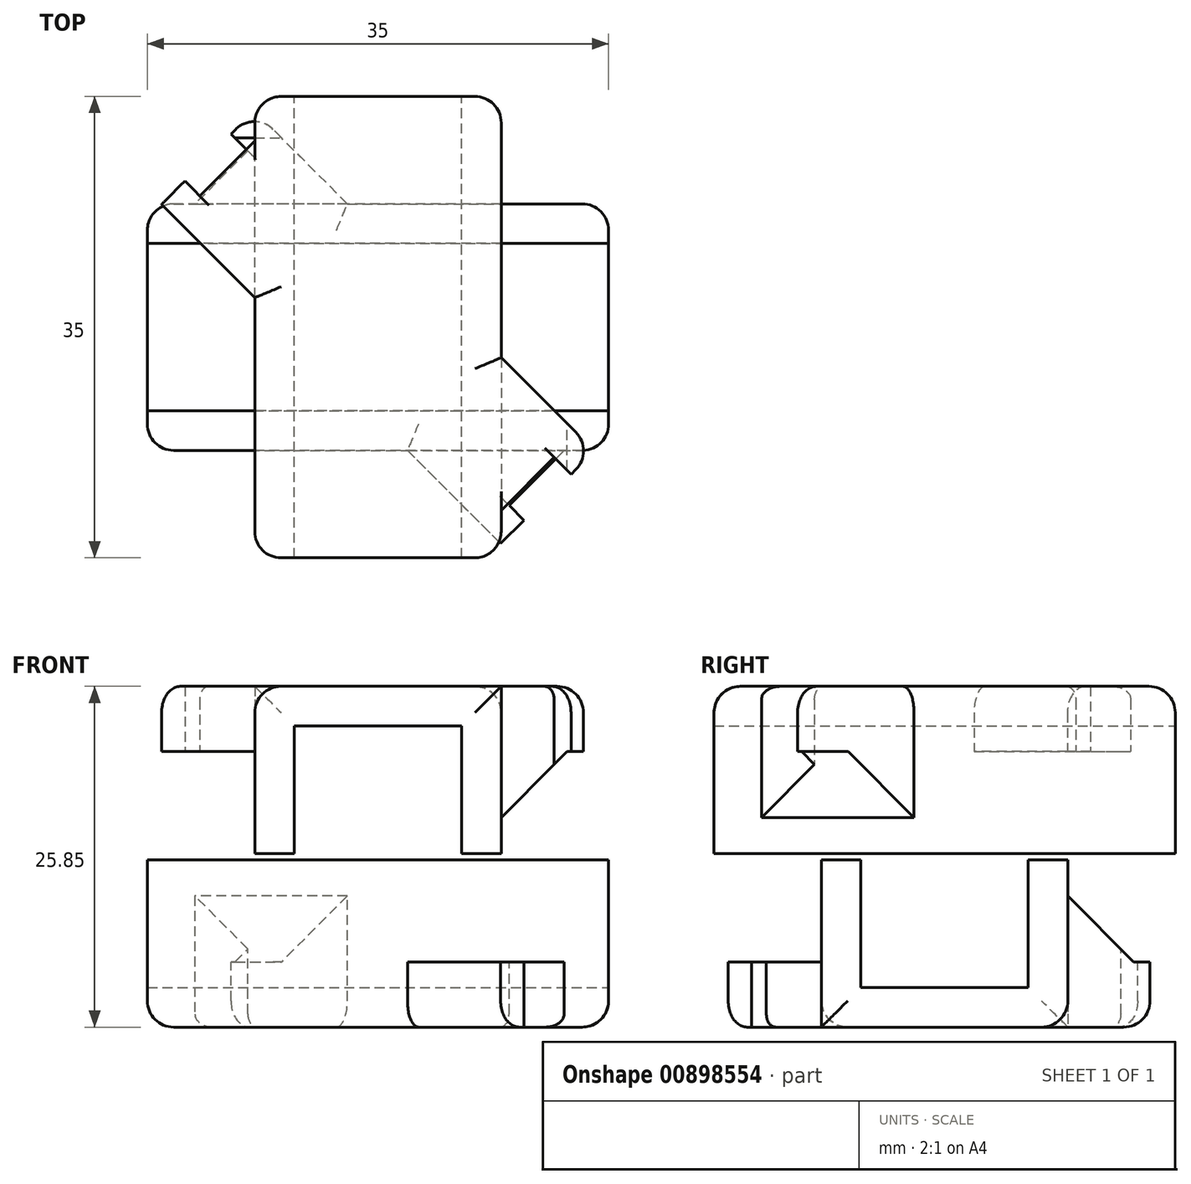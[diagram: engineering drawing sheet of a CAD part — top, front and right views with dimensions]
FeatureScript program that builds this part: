
annotation { "Feature Type Name" : "Feature", "Feature Type Description" : "" }
export const myFeature = defineFeature(function(context is Context, id is Id, definition is map)
    precondition{}
    {
        {
            var Q0;
            Q0=qCreatedBy(makeId("Front.planeOp"),FACE);
            var sketch = newSketch(context, id + "F0", { "sketchPlane" : qUnion([Q0])});
            skLineSegment(sketch, "E0.bottom", {"start": v(6.35, -6.35) * mm, "end": v(-6.35, -6.35) * mm});
            skLineSegment(sketch, "E0.top", {"start": v(6.35, 6.35) * mm, "end": v(-6.35, 6.35) * mm});
            skLineSegment(sketch, "E0.left", {"start": v(6.35, -6.35) * mm, "end": v(6.35, 6.35) * mm});
            skLineSegment(sketch, "E0.right", {"start": v(-6.35, -6.35) * mm, "end": v(-6.35, 6.35) * mm});
            skPoint(sketch, "E0.middle", {"position": v(0, 0) * mm});
            skLineSegment(sketch, "E1.0", {"start": v(9.35, -9.35) * mm, "end": v(-9.35, -9.35) * mm});
            skLineSegment(sketch, "E1.1", {"start": v(9.35, -9.35) * mm, "end": v(9.35, 9.35) * mm});
            skLineSegment(sketch, "E1.2", {"start": v(9.35, 9.35) * mm, "end": v(-9.35, 9.35) * mm});
            skLineSegment(sketch, "E1.3", {"start": v(-9.35, -9.35) * mm, "end": v(-9.35, 9.35) * mm});
            skLineSegment(sketch, "E2", {"start": v(0, 0) * mm, "end": v(0, 32.23) * mm, "construction": true});
            skSolve(sketch);
        }
        {
            var Q0;
            Q0 = qSketchRegion(id + "F0", true);
            extrude(context, id + "F1", {"entities" : qUnion([Q0]), "depth" : 35 * mm, "offsetDistance" : 25 * mm, "symmetric" : true});
        }
        {
            var Q0;
            Q0=qCreatedBy(makeId("Front.planeOp"),FACE);
            var sketch = newSketch(context, id + "F2", { "sketchPlane" : qUnion([Q0])});
            skLineSegment(sketch, "E3.bottom", {"start": v(6.35, -6.35) * mm, "end": v(-6.35, -6.35) * mm, "construction": true});
            skLineSegment(sketch, "E3.top", {"start": v(6.35, 6.35) * mm, "end": v(-6.35, 6.35) * mm, "construction": true});
            skLineSegment(sketch, "E3.left", {"start": v(6.35, -6.35) * mm, "end": v(6.35, 6.35) * mm, "construction": true});
            skLineSegment(sketch, "E3.right", {"start": v(-6.35, -6.35) * mm, "end": v(-6.35, 6.35) * mm, "construction": true});
            skPoint(sketch, "E3.middle", {"position": v(0, 0) * mm});
            skLineSegment(sketch, "E4.bottom", {"start": v(20.53, -3.33) * mm, "end": v(-20.53, -3.33) * mm});
            skLineSegment(sketch, "E4.top", {"start": v(20.53, -26.42) * mm, "end": v(-20.53, -26.42) * mm});
            skLineSegment(sketch, "E4.left", {"start": v(20.53, -3.33) * mm, "end": v(20.53, -26.42) * mm});
            skLineSegment(sketch, "E4.right", {"start": v(-20.53, -3.33) * mm, "end": v(-20.53, -26.42) * mm});
            skPoint(sketch, "E4.middle", {"position": v(0, -14.87) * mm});
            skSolve(sketch);
        }
        {
            var Q0;
            Q0 = qSketchRegion(id + "F2", true);
            extrude(context, id + "F3", {"entities" : qUnion([Q0]), "operationType" : NewBodyOperationType.REMOVE, "depth" : 39.8 * mm, "offsetDistance" : 25 * mm, "symmetric" : true});
        }
        {
            var Q0;
            Q0=qCreatedBy(makeId("Top.planeOp"),FACE);
            var sketch = newSketch(context, id + "F4", { "sketchPlane" : qUnion([Q0])});
            skLineSegment(sketch, "E5.bottom", {"start": v(-9.35, 16.38) * mm, "end": v(-16.42, 9.3) * mm});
            skLineSegment(sketch, "E5.top", {"start": v(16.42, -9.39) * mm, "end": v(9.35, -16.46) * mm});
            skLineSegment(sketch, "E5.left", {"start": v(-9.35, 16.38) * mm, "end": v(16.42, -9.39) * mm});
            skLineSegment(sketch, "E5.right", {"start": v(-16.42, 9.3) * mm, "end": v(9.35, -16.46) * mm});
            skPoint(sketch, "E5.middle", {"position": v(0, -0.04) * mm});
            skLineSegment(sketch, "E6.bottom", {"start": v(-10, 13.49) * mm, "end": v(-13.53, 9.95) * mm});
            skLineSegment(sketch, "E6.right", {"start": v(-13.53, 9.95) * mm, "end": v(-15.78, 12.2) * mm});
            skPoint(sketch, "E6.middle", {"position": v(-12.89, 12.85) * mm});
            skLineSegment(sketch, "E7.top", {"start": v(13.37, -9.87) * mm, "end": v(9.83, -13.4) * mm});
            skLineSegment(sketch, "E7.left", {"start": v(15.93, -12.44) * mm, "end": v(13.37, -9.87) * mm});
            skPoint(sketch, "E7.middle", {"position": v(12.88, -12.92) * mm});
            skLineSegment(sketch, "E8", {"start": v(-10, 13.49) * mm, "end": v(-5.5, 17.98) * mm});
            skLineSegment(sketch, "E9", {"start": v(9.83, -13.4) * mm, "end": v(5.07, -18.17) * mm});
            skLineSegment(sketch, "E10", {"start": v(0, 0) * mm, "end": v(0, 33.96) * mm, "construction": true});
            skSolve(sketch);
        }
        {
            var Q0;
            {var subQ15=sQuery(id+"F4.wireOp",EDGE,"E6.bottom");Q0=makeQuery(id+"F4.imprint","IMPRINT",FACE,{"disambiguationData":[TD([[makeQuery(id+"F4.imprint","IMPRINT",EDGE,{"derivedFrom":subQ15}),1.0]])]});}
            extrude(context, id + "F5", {"entities" : qUnion([Q0]), "operationType" : NewBodyOperationType.ADD, "depth" : ((12.7 / 2) + 3) * mm, "offsetDistance" : 25 * mm, "hasSecondDirection" : true, "secondDirectionOppositeDirection" : false, "secondDirectionDepth" : 4.4 * mm});
        }
        {
            var Q0;
            Q0=makeQuery(id+"F5.opExtrude","CAP_EDGE",EDGE,{"disambiguationData":[OSD([sQuery(id+"F4.wireOp",EDGE,"E7.top"),sQuery(id+"F4.wireOp",EDGE,"E9")])],"isStart":false});
            var Q1;
            Q1=makeQuery(id+"F5.opExtrude","CAP_EDGE",EDGE,{"disambiguationData":[OSD([sQuery(id+"F4.wireOp",EDGE,"E6.bottom"),sQuery(id+"F4.wireOp",EDGE,"E8")])],"isStart":false});
            fillet(context, id + "F6", {"entities" : qUnion([Q0, Q1]), "radius" : 1 * mm, "tangentPropagation" : true, "allowEdgeOverflow" : false});
        }
        {
            var Q0;
            Q0=makeQuery(id+"F0.imprint","IMPRINT",FACE,{"disambiguationData":[TD([[makeQuery(id+"F0.imprint","IMPRINT",EDGE,{"derivedFrom":sQuery(id+"F0.wireOp",EDGE,"E0.bottom")}),-1.0]])]});
            var Q1;
            Q1=sQuery(id+"F0.wireOp",EDGE,"E0.bottom");
            var Q2;
            Q2=sQuery(id+"F0.wireOp",EDGE,"E0.top");
            var Q3;
            Q3=sQuery(id+"F0.wireOp",EDGE,"E0.right");
            var Q4;
            Q4=sQuery(id+"F0.wireOp",EDGE,"E0.left");
            extrude(context, id + "F7", {"entities" : qUnion([Q0]), "operationType" : NewBodyOperationType.REMOVE, "surfaceEntities" : qUnion([Q1, Q2, Q3, Q4]), "depth" : 50 * mm, "offsetDistance" : 25 * mm, "symmetric" : true});
        }
        {
            var Q0;
            Q0=makeQuery(id+"F5.boolean.opBoolean","INTERSECT",EDGE,{"derivedFrom":[makeQuery(id+"F1.opExtrude","SWEPT_FACE",FACE,{"disambiguationData":[OSD([sQuery(id+"F0.wireOp",EDGE,"E1.1")])]}),makeQuery(id+"F5.opExtrude","CAP_FACE",FACE,{"disambiguationData":[OSD([sQuery(id+"F4.wireOp",EDGE,"E5.bottom"),sQuery(id+"F4.wireOp",EDGE,"E5.top"),sQuery(id+"F4.wireOp",EDGE,"E5.left"),sQuery(id+"F4.wireOp",EDGE,"E5.right"),sQuery(id+"F4.wireOp",EDGE,"E6.bottom"),sQuery(id+"F4.wireOp",EDGE,"E6.right"),sQuery(id+"F4.wireOp",EDGE,"E7.top"),sQuery(id+"F4.wireOp",EDGE,"E7.left"),sQuery(id+"F4.wireOp",EDGE,"E8"),sQuery(id+"F4.wireOp",EDGE,"E9")])],"isStart":true})]});
            chamfer(context, id + "F8", {"entities" : qUnion([Q0]), "width" : 5 * mm, "tangentPropagation" : true});
        }
        {
            var Q0;
            {var subQ0=sQuery(id+"F4.wireOp",EDGE,"E5.left");var subQ1=sQuery(id+"F0.wireOp",EDGE,"E1.2");var subQ2=sQuery(id+"F0.wireOp",EDGE,"E1.1");Q0=makeQuery(id+"F5.boolean.opBoolean","SPLIT",EDGE,{"disambiguationData":[TD([makeQuery(id+"F5.opExtrude","SWEPT_FACE",FACE,{"disambiguationData":[OSD([subQ0])]})])],"derivedFrom":makeQuery(id+"F1.opExtrude","SWEPT_EDGE",EDGE,{"disambiguationData":[OSD([subQ2,subQ1])]})});}
            var Q1;
            {var subQ0=sQuery(id+"F4.wireOp",EDGE,"E5.right");var subQ1=sQuery(id+"F0.wireOp",EDGE,"E1.2");var subQ2=sQuery(id+"F0.wireOp",EDGE,"E1.3");Q1=makeQuery(id+"F5.boolean.opBoolean","SPLIT",EDGE,{"disambiguationData":[TD([makeQuery(id+"F5.opExtrude","SWEPT_FACE",FACE,{"disambiguationData":[OSD([subQ0])]})])],"derivedFrom":makeQuery(id+"F1.opExtrude","SWEPT_EDGE",EDGE,{"disambiguationData":[OSD([subQ1,subQ2])]})});}
            var Q2;
            Q2=makeQuery(id+"F1.opExtrude","CAP_EDGE",EDGE,{"disambiguationData":[OSD([sQuery(id+"F0.wireOp",EDGE,"E1.2")])],"isStart":false});
            var Q3;
            Q3=makeQuery(id+"F1.opExtrude","CAP_EDGE",EDGE,{"disambiguationData":[OSD([sQuery(id+"F0.wireOp",EDGE,"E1.2")])],"isStart":true});
            var Q4;
            Q4=makeQuery(id+"F5.opExtrude","SWEPT_EDGE",EDGE,{"disambiguationData":[OSD([sQuery(id+"F4.wireOp",EDGE,"E5.top"),sQuery(id+"F4.wireOp",EDGE,"E5.left")])]});
            var Q5;
            Q5=makeQuery(id+"F5.opExtrude","CAP_EDGE",EDGE,{"disambiguationData":[OSD([sQuery(id+"F4.wireOp",EDGE,"E5.left")])],"isStart":false});
            var Q6;
            Q6=makeQuery(id+"F5.opExtrude","CAP_EDGE",EDGE,{"disambiguationData":[OSD([sQuery(id+"F4.wireOp",EDGE,"E5.right")])],"isStart":false});
            var Q7;
            Q7=makeQuery(id+"F5.opExtrude","CAP_EDGE",EDGE,{"disambiguationData":[OSD([sQuery(id+"F4.wireOp",EDGE,"E5.top")])],"isStart":false});
            var Q8;
            Q8=makeQuery(id+"F1.opExtrude","CAP_EDGE",EDGE,{"disambiguationData":[OSD([sQuery(id+"F0.wireOp",EDGE,"E1.1")])],"isStart":false});
            var Q9;
            Q9=makeQuery(id+"F1.opExtrude","CAP_EDGE",EDGE,{"disambiguationData":[OSD([sQuery(id+"F0.wireOp",EDGE,"E1.3")])],"isStart":false});
            var Q10;
            Q10=makeQuery(id+"F1.opExtrude","CAP_EDGE",EDGE,{"disambiguationData":[OSD([sQuery(id+"F0.wireOp",EDGE,"E1.1")])],"isStart":true});
            var Q11;
            Q11=makeQuery(id+"F1.opExtrude","CAP_EDGE",EDGE,{"disambiguationData":[OSD([sQuery(id+"F0.wireOp",EDGE,"E1.3")])],"isStart":true});
            fillet(context, id + "F9", {"entities" : qUnion([Q0, Q1, Q2, Q3, Q4, Q5, Q6, Q7, Q8, Q9, Q10, Q11]), "radius" : 2 * mm, "tangentPropagation" : true, "allowEdgeOverflow" : false});
        }
        {
            var Q0;
            Q0=makeQuery(id+"F1.opExtrude","SWEPT_BODY",BODY,{"disambiguationData":[OSD([sQuery(id+"F0.wireOp",EDGE,"E0.bottom"),sQuery(id+"F0.wireOp",EDGE,"E0.top"),sQuery(id+"F0.wireOp",EDGE,"E0.left"),sQuery(id+"F0.wireOp",EDGE,"E0.right"),sQuery(id+"F0.wireOp",EDGE,"E1.0"),sQuery(id+"F0.wireOp",EDGE,"E1.1"),sQuery(id+"F0.wireOp",EDGE,"E1.2"),sQuery(id+"F0.wireOp",EDGE,"E1.3")])]});
            transform(context, id + "F10", {"entities" : qUnion([Q0]), "transformType" : TransformType.TRANSLATION_3D, "dx" : 0 * mm, "dy" : 0 * mm, "dz" : -15.6 * mm, "makeCopy" : true});
        }
        {
            var Q0;
            Q0=makeQuery(id+"F10.opPattern","COPY",BODY,{"derivedFrom":makeQuery(id+"F1.opExtrude","SWEPT_BODY",BODY,{"disambiguationData":[OSD([sQuery(id+"F0.wireOp",EDGE,"E0.bottom"),sQuery(id+"F0.wireOp",EDGE,"E0.top"),sQuery(id+"F0.wireOp",EDGE,"E0.left"),sQuery(id+"F0.wireOp",EDGE,"E0.right"),sQuery(id+"F0.wireOp",EDGE,"E1.0"),sQuery(id+"F0.wireOp",EDGE,"E1.1"),sQuery(id+"F0.wireOp",EDGE,"E1.2"),sQuery(id+"F0.wireOp",EDGE,"E1.3")])]}),"instanceName":"1"});
            var Q1;
            Q1=sQuery(id+"F0.wireOp",EDGE,"E2");
            transform(context, id + "F11", {"entities" : qUnion([Q0]), "transformType" : TransformType.ROTATION, "transformAxis" : qUnion([Q1]), "angle" : 90 * degree, "makeCopy" : false});
        }
        {
            var Q0;
            Q0=qCreatedBy(makeId("Right.planeOp"),FACE);
            var sketch = newSketch(context, id + "F12", { "sketchPlane" : qUnion([Q0])});
            skLineSegment(sketch, "E11", {"start": v(-23.85, -11.37) * mm, "end": v(25.43, -11.37) * mm, "construction": true});
            skSolve(sketch);
        }
        {
            var Q0;
            Q0=makeQuery(id+"F10.opPattern","COPY",BODY,{"derivedFrom":makeQuery(id+"F1.opExtrude","SWEPT_BODY",BODY,{"disambiguationData":[OSD([sQuery(id+"F0.wireOp",EDGE,"E0.bottom"),sQuery(id+"F0.wireOp",EDGE,"E0.top"),sQuery(id+"F0.wireOp",EDGE,"E0.left"),sQuery(id+"F0.wireOp",EDGE,"E0.right"),sQuery(id+"F0.wireOp",EDGE,"E1.0"),sQuery(id+"F0.wireOp",EDGE,"E1.1"),sQuery(id+"F0.wireOp",EDGE,"E1.2"),sQuery(id+"F0.wireOp",EDGE,"E1.3")])]}),"instanceName":"1"});
            var Q1;
            Q1=sQuery(id+"F12.wireOp",EDGE,"E11");
            transform(context, id + "F13", {"entities" : qUnion([Q0]), "transformType" : TransformType.ROTATION, "transformAxis" : qUnion([Q1]), "angle" : 180 * degree, "makeCopy" : false});
        }
    });
